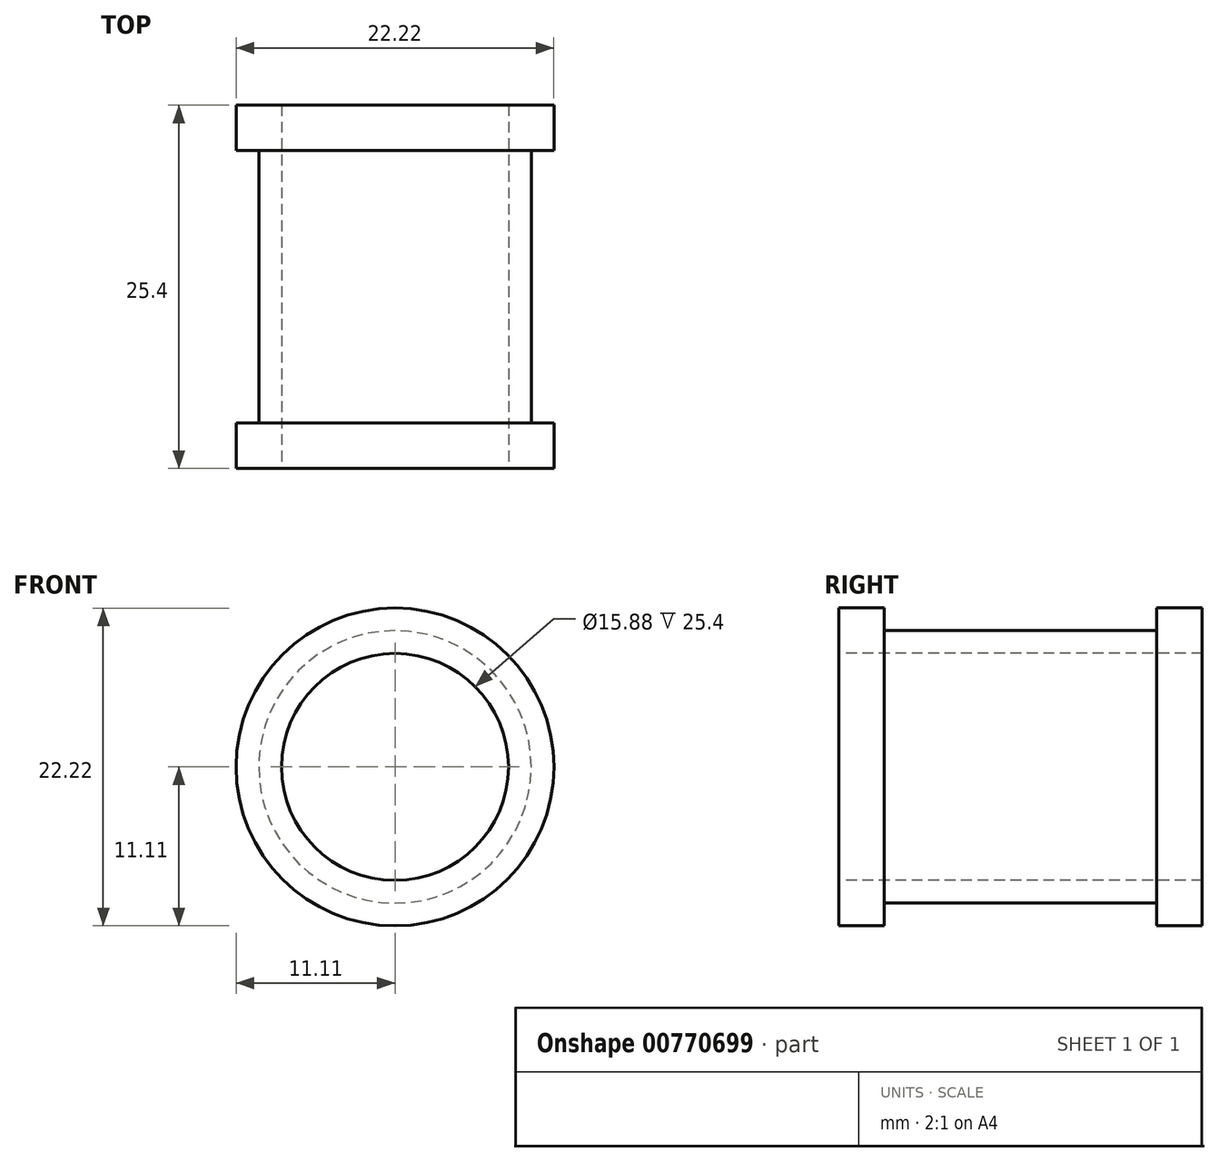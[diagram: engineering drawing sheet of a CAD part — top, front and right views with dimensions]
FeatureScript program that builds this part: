
annotation { "Feature Type Name" : "Feature", "Feature Type Description" : "" }
export const myFeature = defineFeature(function(context is Context, id is Id, definition is map)
    precondition{}
    {
        {
            var Q0;
            Q0=qCreatedBy(makeId("Right.planeOp"),FACE);
            var sketch = newSketch(context, id + "F0", { "sketchPlane" : qUnion([Q0])});
            skLineSegment(sketch, "E0", {"start": v(0, 0) * mm, "end": v(19.88, 0) * mm, "construction": true});
            skLineSegment(sketch, "E1", {"start": v(0, 11.11) * mm, "end": v(0, 7.94) * mm});
            skLineSegment(sketch, "E2", {"start": v(0, 7.94) * mm, "end": v(25.4, 7.94) * mm});
            skLineSegment(sketch, "E3", {"start": v(25.4, 7.94) * mm, "end": v(25.4, 11.11) * mm});
            skLineSegment(sketch, "E4", {"start": v(25.4, 11.11) * mm, "end": v(22.23, 11.11) * mm});
            skLineSegment(sketch, "E5", {"start": v(22.23, 11.11) * mm, "end": v(22.23, 9.53) * mm});
            skLineSegment(sketch, "E6", {"start": v(22.23, 9.53) * mm, "end": v(3.18, 9.53) * mm});
            skLineSegment(sketch, "E7", {"start": v(3.18, 9.53) * mm, "end": v(3.18, 11.11) * mm});
            skLineSegment(sketch, "E8", {"start": v(3.18, 11.11) * mm, "end": v(0, 11.11) * mm});
            skSolve(sketch);
        }
        {
            var Q0;
            Q0 = qSketchRegion(id + "F0", true);
            var Q1;
            Q1=sQuery(id+"F0.wireOp",EDGE,"E0");
            revolve(context, id + "F1", {"surfaceOperationType" : NewSurfaceOperationType.NEW, "entities" : qUnion([Q0]), "axis" : qUnion([Q1]), "revolveType" : RevolveType.FULL});
        }
    });
